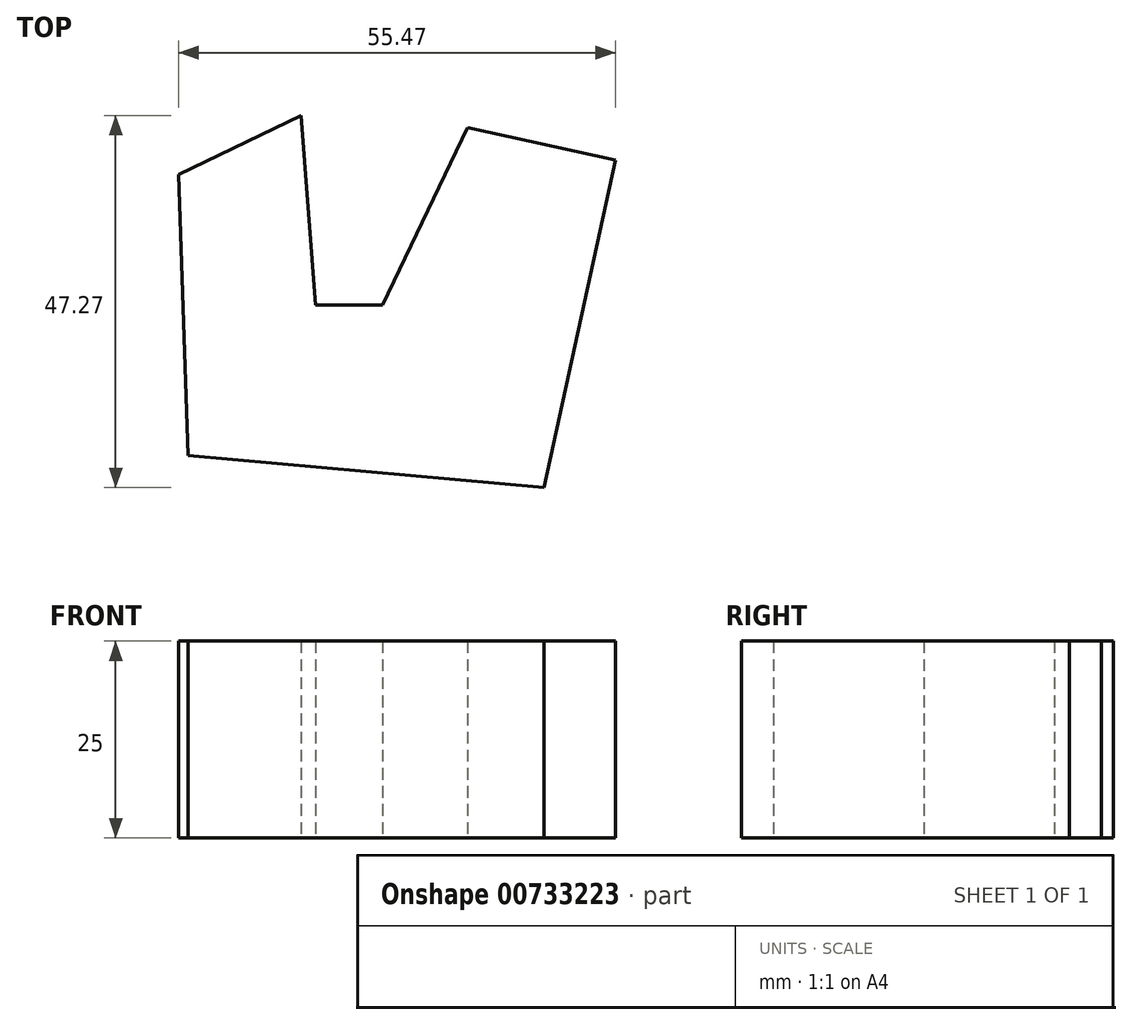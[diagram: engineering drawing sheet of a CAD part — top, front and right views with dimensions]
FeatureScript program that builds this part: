
annotation { "Feature Type Name" : "Feature", "Feature Type Description" : "" }
export const myFeature = defineFeature(function(context is Context, id is Id, definition is map)
    precondition{}
    {
        {
            var Q0;
            Q0=qCreatedBy(makeId("Top.planeOp"),FACE);
            var sketch = newSketch(context, id + "F0", { "sketchPlane" : qUnion([Q0])});
            skLineSegment(sketch, "E0", {"start": v(-25.87, 28.97) * mm, "end": v(-24.67, -6.7) * mm});
            skLineSegment(sketch, "E1", {"start": v(-24.67, -6.7) * mm, "end": v(20.55, -10.8) * mm});
            skLineSegment(sketch, "E2", {"start": v(20.55, -10.8) * mm, "end": v(29.6, 30.85) * mm});
            skLineSegment(sketch, "E3", {"start": v(29.6, 30.85) * mm, "end": v(10.79, 34.93) * mm});
            skLineSegment(sketch, "E4", {"start": v(10.79, 34.93) * mm, "end": v(0, 12.42) * mm});
            skLineSegment(sketch, "E5", {"start": v(0, 12.42) * mm, "end": v(-8.46, 12.42) * mm});
            skLineSegment(sketch, "E6", {"start": v(-8.46, 12.42) * mm, "end": v(-10.34, 36.48) * mm});
            skLineSegment(sketch, "E7", {"start": v(-10.34, 36.48) * mm, "end": v(-25.87, 28.97) * mm});
            skSolve(sketch);
        }
        {
            var Q0;
            Q0 = qSketchRegion(id + "F0", true);
            extrude(context, id + "F1", {"entities" : qUnion([Q0]), "depth" : 25 * mm, "offsetDistance" : 25 * mm});
        }
    });
